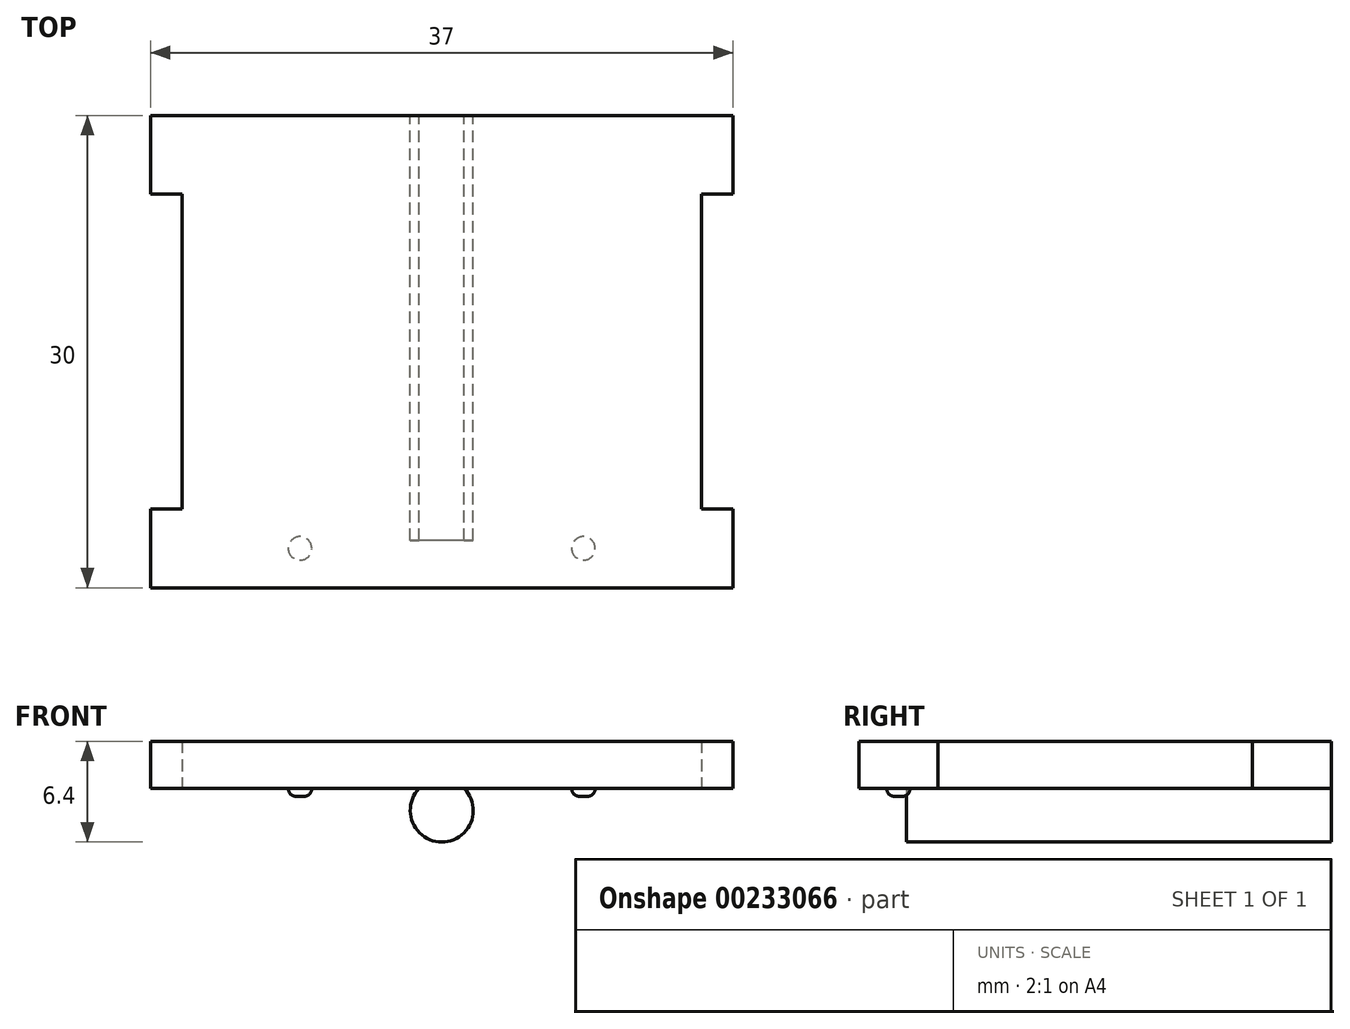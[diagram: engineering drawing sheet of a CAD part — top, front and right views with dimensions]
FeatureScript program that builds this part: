
annotation { "Feature Type Name" : "Feature", "Feature Type Description" : "" }
export const myFeature = defineFeature(function(context is Context, id is Id, definition is map)
    precondition{}
    {
        {
            var Q0;
            Q0=qCreatedBy(makeId("Top.planeOp"),FACE);
            var sketch = newSketch(context, id + "F0", { "sketchPlane" : qUnion([Q0])});
            skLineSegment(sketch, "E0.bottom", {"start": v(5.26, 9.22) * mm, "end": v(-1.74, 9.22) * mm});
            skLineSegment(sketch, "E0.top", {"start": v(5.26, -10.78) * mm, "end": v(-1.74, -10.78) * mm});
            skLineSegment(sketch, "E0.left", {"start": v(5.26, 9.22) * mm, "end": v(5.26, -10.78) * mm});
            skLineSegment(sketch, "E0.right", {"start": v(-1.74, 9.22) * mm, "end": v(-1.74, -10.78) * mm});
            skPoint(sketch, "E0.middle", {"position": v(1.76, -0.78) * mm});
            skLineSegment(sketch, "E1.bottom", {"start": v(20.26, 9.22) * mm, "end": v(-16.74, 9.22) * mm});
            skLineSegment(sketch, "E1.top", {"start": v(20.26, 14.22) * mm, "end": v(-16.74, 14.22) * mm});
            skLineSegment(sketch, "E1.left", {"start": v(20.26, 9.22) * mm, "end": v(20.26, 14.22) * mm});
            skLineSegment(sketch, "E1.right", {"start": v(-16.74, 9.22) * mm, "end": v(-16.74, 14.22) * mm});
            skPoint(sketch, "E1.middle", {"position": v(1.76, 11.72) * mm});
            skPoint(sketch, "E1.middle.positionSnap0", {"position": v(1.76, 9.22) * mm});
            skPoint(sketch, "E1.centerSnap0", {"position": v(1.76, 9.22) * mm});
            skLineSegment(sketch, "E2.bottom", {"start": v(-12.74, 10.72) * mm, "end": v(-14.74, 10.72) * mm});
            skLineSegment(sketch, "E2.top", {"start": v(-12.74, -12.28) * mm, "end": v(-14.74, -12.28) * mm});
            skLineSegment(sketch, "E2.left", {"start": v(-12.74, 10.72) * mm, "end": v(-12.74, -12.28) * mm});
            skLineSegment(sketch, "E2.right", {"start": v(-14.74, 10.72) * mm, "end": v(-14.74, -12.28) * mm});
            skPoint(sketch, "E2.middle", {"position": v(-13.74, -0.78) * mm});
            skLineSegment(sketch, "E3.MirrorCS", {"start": v(-16.74, -10.78) * mm, "end": v(-16.74, -15.78) * mm});
            skLineSegment(sketch, "E4.MirrorCS", {"start": v(20.26, -15.78) * mm, "end": v(-16.74, -15.78) * mm});
            skLineSegment(sketch, "E5.MirrorCS", {"start": v(20.26, -10.78) * mm, "end": v(-16.74, -10.78) * mm});
            skLineSegment(sketch, "E6.MirrorCS", {"start": v(20.26, -10.78) * mm, "end": v(20.26, -15.78) * mm});
            skLineSegment(sketch, "E7.MirrorCS", {"start": v(-14.74, -12.28) * mm, "end": v(-14.74, 10.72) * mm});
            skLineSegment(sketch, "E8.MirrorCS", {"start": v(16.26, -12.28) * mm, "end": v(18.26, -12.28) * mm});
            skLineSegment(sketch, "E9.MirrorCS", {"start": v(16.26, 10.72) * mm, "end": v(18.26, 10.72) * mm});
            skLineSegment(sketch, "E10.MirrorCS", {"start": v(18.26, -12.28) * mm, "end": v(18.26, 10.72) * mm});
            skLineSegment(sketch, "E11.MirrorCS", {"start": v(16.26, 10.72) * mm, "end": v(16.26, -12.28) * mm});
            skSolve(sketch);
        }
        {
            var Q0;
            Q0 = qSketchRegion(id + "F0", true);
            var Q1;
            {var subQ0=sQuery(id+"F0.wireOp",EDGE,"E0.right");Q1=makeQuery(id+"F0.imprint","IMPRINT",FACE,{"disambiguationData":[TD([[makeQuery(id+"F0.imprint","IMPRINT",EDGE,{"derivedFrom":subQ0}),-1.0]])]});}
            var Q2;
            {var subQ0=sQuery(id+"F0.wireOp",EDGE,"E0.left");Q2=makeQuery(id+"F0.imprint","IMPRINT",FACE,{"disambiguationData":[TD([[makeQuery(id+"F0.imprint","IMPRINT",EDGE,{"derivedFrom":subQ0}),-1.0]])]});}
            var Q3;
            {var subQ0=sQuery(id+"F0.wireOp",EDGE,"E0.left");Q3=makeQuery(id+"F0.imprint","IMPRINT",FACE,{"disambiguationData":[TD([[makeQuery(id+"F0.imprint","IMPRINT",EDGE,{"derivedFrom":subQ0}),1.0]])]});}
            extrude(context, id + "F1", {"entities" : qUnion([Q0, Q1, Q2, Q3]), "depth" : 3 * mm});
        }
        {
            var Q0;
            Q0=makeQuery(id+"F1.opExtrude","SWEPT_FACE",FACE,{"disambiguationData":[OSD([sQuery(id+"F0.wireOp",EDGE,"E1.top")])]});
            var sketch = newSketch(context, id + "F2", { "sketchPlane" : qUnion([Q0])});
            skCircle(sketch, "E12", {"center": v(0, -1.4) * mm, "radius": 1.98 * mm});
            skSolve(sketch);
        }
        {
            var Q0;
            {var subQ0=sQuery(id+"F2.wireOp",EDGE,"E12");var subQ1=makeQuery(id+"F1.opExtrude","CAP_EDGE",EDGE,{"disambiguationData":[OSD([sQuery(id+"F0.wireOp",EDGE,"E1.top")])],"isStart":true});var subQ2=makeQuery(id+"F2.imprint","INTERSECT",VERTEX,{"disambiguationData":[OD(0.0)],"derivedFrom":[subQ1,subQ0]});Q0=makeQuery(id+"F2.imprint","IMPRINT",FACE,{"disambiguationData":[TD([[makeQuery(id+"F2.imprint","IMPRINT",EDGE,{"disambiguationData":[TD([[subQ2,-1.0]])],"derivedFrom":subQ0}),1.0]])]});}
            extrude(context, id + "F3", {"entities" : qUnion([Q0]), "oppositeDirection" : true, "depth" : 26.5 * mm});
        }
        {
            var Q0;
            Q0=makeQuery(id+"F3.opExtrude","SWEPT_BODY",BODY,{"disambiguationData":[OSD([sQuery(id+"F0.wireOp",EDGE,"E1.top"),sQuery(id+"F2.wireOp",EDGE,"E12")])]});
            deleteBodies(context, id + "F4", {"entities" : qUnion([Q0])});
        }
        {
            var Q0;
            Q0=makeQuery(id+"F1.opExtrude","SWEPT_FACE",FACE,{"disambiguationData":[OSD([sQuery(id+"F0.wireOp",EDGE,"E1.top")])]});
            var sketch = newSketch(context, id + "F5", { "sketchPlane" : qUnion([Q0])});
            skCircle(sketch, "E13", {"center": v(-1.76, -1.4) * mm, "radius": 2 * mm});
            skPoint(sketch, "E13.centerSnap0", {"position": v(-1.76, 0) * mm});
            skSolve(sketch);
        }
        {
            var Q0;
            Q0 = qSketchRegion(id + "F5", true);
            extrude(context, id + "F6", {"entities" : qUnion([Q0]), "operationType" : NewBodyOperationType.ADD, "oppositeDirection" : true, "depth" : 27 * mm});
        }
        {
            var Q0;
            Q0=makeQuery(id+"F1.opExtrude","CAP_FACE",FACE,{"disambiguationData":[OSD([sQuery(id+"F0.wireOp",EDGE,"E1.bottom"),sQuery(id+"F0.wireOp",EDGE,"E1.top"),sQuery(id+"F0.wireOp",EDGE,"E1.left"),sQuery(id+"F0.wireOp",EDGE,"E1.right"),sQuery(id+"F0.wireOp",EDGE,"E3.MirrorCS"),sQuery(id+"F0.wireOp",EDGE,"E4.MirrorCS"),sQuery(id+"F0.wireOp",EDGE,"E5.MirrorCS"),sQuery(id+"F0.wireOp",EDGE,"E6.MirrorCS"),sQuery(id+"F0.wireOp",EDGE,"E7.MirrorCS"),sQuery(id+"F0.wireOp",EDGE,"E10.MirrorCS")])],"isStart":true});
            var sketch = newSketch(context, id + "F7", { "sketchPlane" : qUnion([Q0])});
            skCircle(sketch, "E14", {"center": v(-7.24, 13.28) * mm, "radius": 0.75 * mm});
            skCircle(sketch, "E15", {"center": v(10.76, 13.28) * mm, "radius": 0.75 * mm});
            skSolve(sketch);
        }
        {
            var Q0;
            Q0 = qSketchRegion(id + "F7", true);
            extrude(context, id + "F8", {"entities" : qUnion([Q0]), "operationType" : NewBodyOperationType.ADD, "depth" : .5 * mm});
        }
        {
            var Q0;
            Q0=makeQuery(id+"F8.opExtrude","CAP_FACE",FACE,{"disambiguationData":[OSD([sQuery(id+"F7.wireOp",EDGE,"E15")])],"isStart":false});
            var Q1;
            Q1=makeQuery(id+"F8.opExtrude","CAP_FACE",FACE,{"disambiguationData":[OSD([sQuery(id+"F7.wireOp",EDGE,"E14")])],"isStart":false});
            fillet(context, id + "F9", {"entities" : qUnion([Q0, Q1]), "radius" : .5 * mm, "tangentPropagation" : true, "allowEdgeOverflow" : false});
        }
    });
